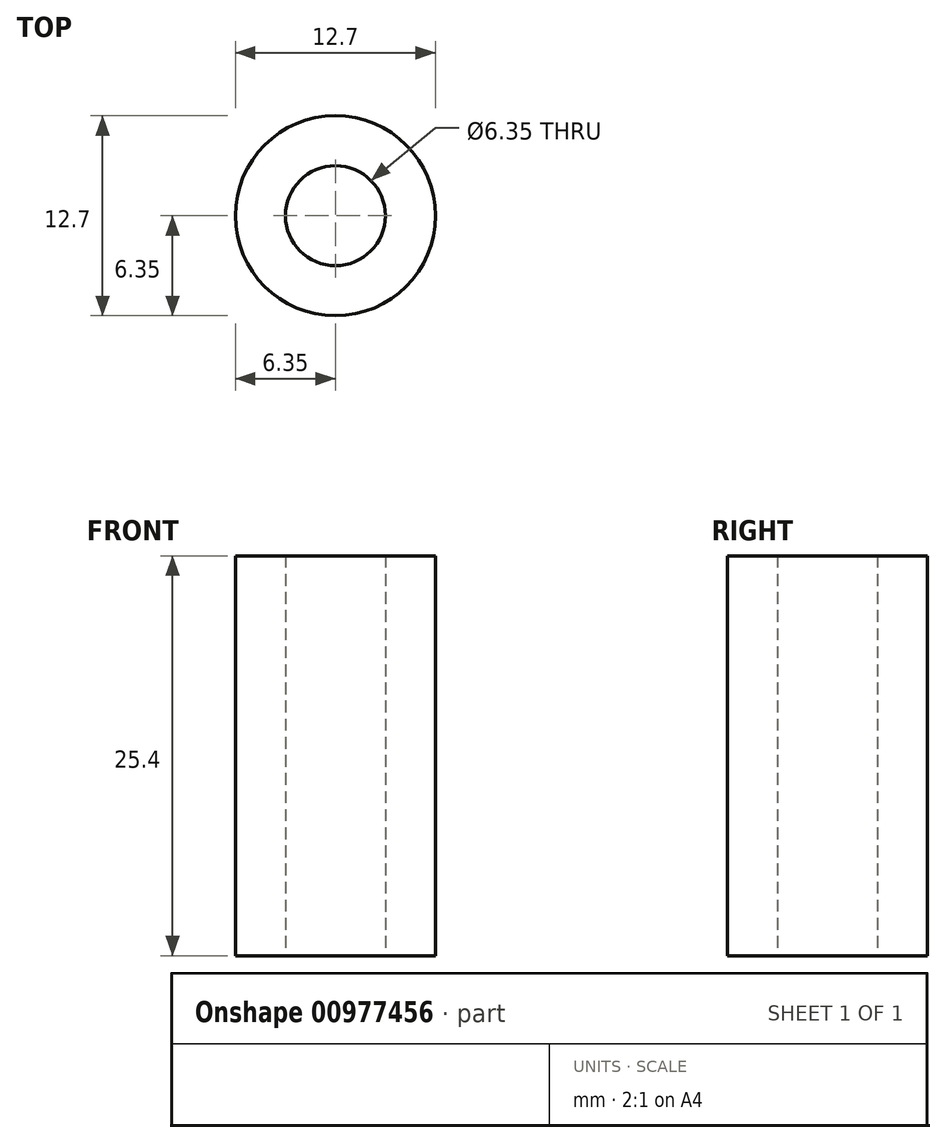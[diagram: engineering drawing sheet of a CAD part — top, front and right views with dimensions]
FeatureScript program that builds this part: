
annotation { "Feature Type Name" : "Feature", "Feature Type Description" : "" }
export const myFeature = defineFeature(function(context is Context, id is Id, definition is map)
    precondition{}
    {
        {
            var Q0;
            Q0=qCreatedBy(makeId("Top.planeOp"),FACE);
            var sketch = newSketch(context, id + "F0", { "sketchPlane" : qUnion([Q0])});
            skCircle(sketch, "E0", {"center": v(0, 0) * mm, "radius": 3.18 * mm});
            skCircle(sketch, "E1", {"center": v(0, 0) * mm, "radius": 6.35 * mm});
            skSolve(sketch);
        }
        {
            var Q0;
            Q0 = qSketchRegion(id + "F0", true);
            extrude(context, id + "F1", {"entities" : qUnion([Q0]), "depth" : 25.4 * mm, "offsetDistance" : 25.4 * mm});
        }
    });
